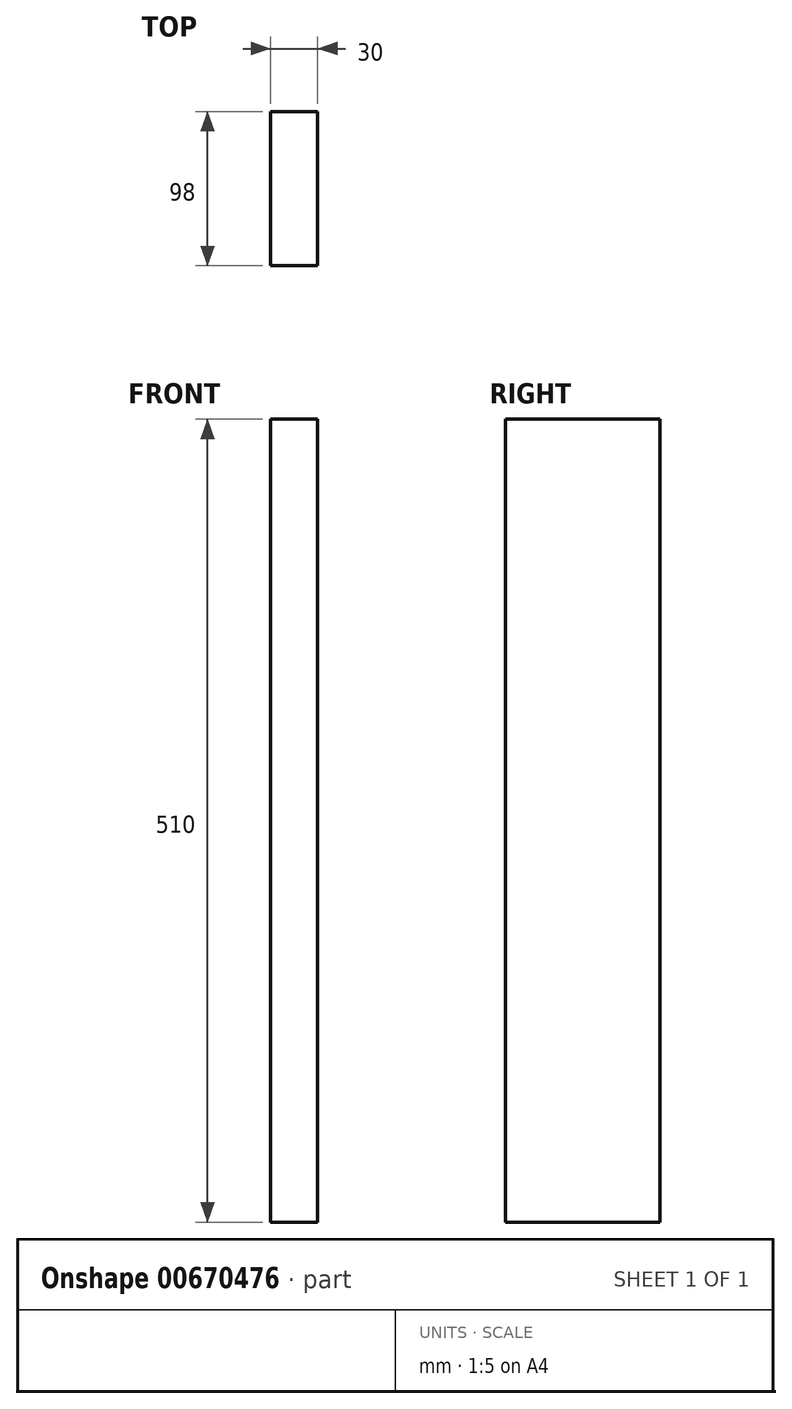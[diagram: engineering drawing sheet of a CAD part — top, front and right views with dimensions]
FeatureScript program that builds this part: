
annotation { "Feature Type Name" : "Feature", "Feature Type Description" : "" }
export const myFeature = defineFeature(function(context is Context, id is Id, definition is map)
    precondition{}
    {
        {
            var Q0;
            Q0=qCreatedBy(makeId("Top.planeOp"),FACE);
            var sketch = newSketch(context, id + "F0", { "sketchPlane" : qUnion([Q0])});
            skLineSegment(sketch, "E0.bottom", {"start": v(15, -49) * mm, "end": v(-15, -49) * mm});
            skLineSegment(sketch, "E0.top", {"start": v(15, 49) * mm, "end": v(-15, 49) * mm});
            skLineSegment(sketch, "E0.left", {"start": v(15, -49) * mm, "end": v(15, 49) * mm});
            skLineSegment(sketch, "E0.right", {"start": v(-15, -49) * mm, "end": v(-15, 49) * mm});
            skPoint(sketch, "E0.middle", {"position": v(0, 0) * mm});
            skSolve(sketch);
        }
        {
            var Q0;
            Q0 = qSketchRegion(id + "F0", true);
            extrude(context, id + "F1", {"entities" : qUnion([Q0]), "depth" : 510 * mm, "offsetDistance" : 25 * mm});
        }
    });
